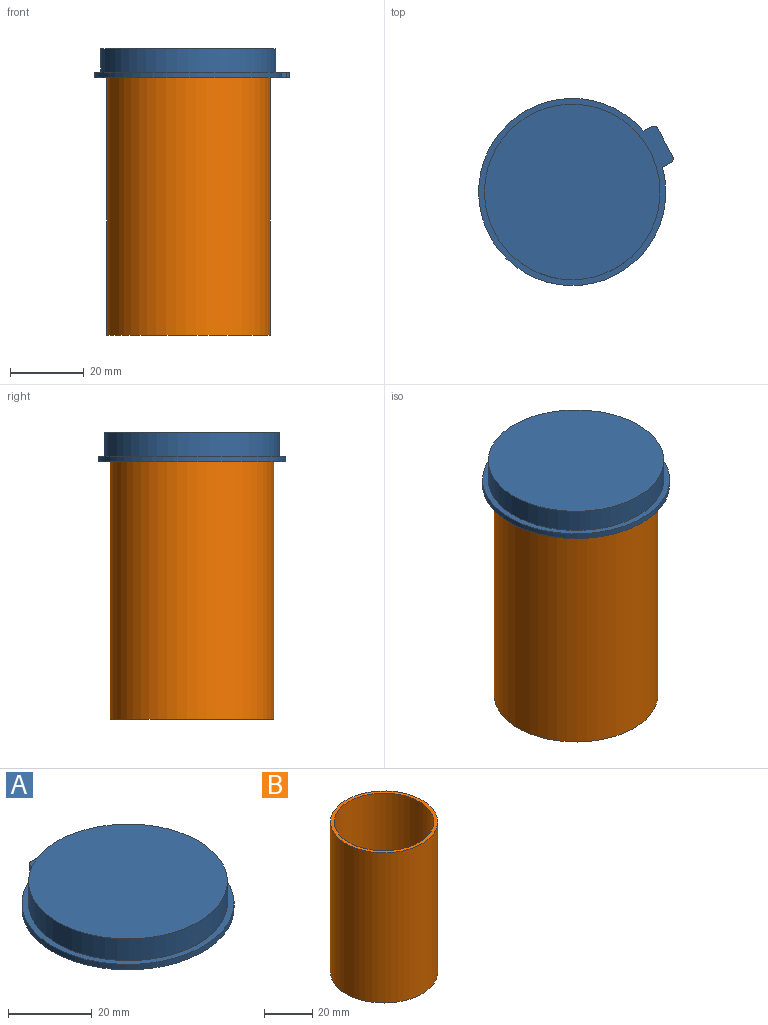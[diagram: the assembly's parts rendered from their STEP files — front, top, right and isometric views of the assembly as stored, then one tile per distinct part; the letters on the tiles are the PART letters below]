
ASSEMBLY  parts=2 mates=1
PART A: 12 faces, bbox 50.8x54x7.9 mm
  f0: cylinder r=23.81mm len=47.63mm, axis (0,0,-1), area 950.1mm2, adj f1,f8
  f1: plane 47.63x47.63mm, normal (0,0,1), area 1781.4mm2, adj f0
  f2: cylinder r=1.27mm len=1.59mm, axis (0,0,-1), area 3.2mm2, adj f3,f7,f8,f9
  f3: plane 8.57x1.59mm, normal (0,1,0), area 13.6mm2, adj f2,f4,f8,f9
  f4: cylinder r=1.27mm len=1.59mm, axis (0,0,-1), area 3.2mm2, adj f3,f5,f8,f9
  f5: plane 2.52x1.59mm, normal (-1,0,0), area 4mm2, adj f4,f6,f8,f9
  f6: cylinder r=25.4mm len=50.8mm, axis (0,0,-1), area 235.6mm2, adj f5,f7,f8,f9
  f7: plane 2.52x1.59mm, normal (1,0,0), area 4mm2, adj f2,f6,f8,f9
  f8: plane 53.98x50.8mm, normal (0,0,1), area 282.3mm2, adj f0,f2,f3,f4,f5,f6,f7
  f9: plane 53.98x50.8mm, normal (0,0,-1), area 511.9mm2, adj f2,f3,f4,f5,f6,f7,f11
  f10: plane 44.45x44.45mm, normal (0,0,-1), area 1551.8mm2, adj f11
  f11: cylinder r=22.23mm len=44.45mm, axis (0,0,-1), area 886.7mm2, adj f9,f10
PART B: 5 faces, bbox 44.5x44.5x76.2 mm
  f0: cylinder r=22.23mm len=76.2mm, axis (0,0,-1), area 10640.9mm2, adj f1,f2
  f1: plane 44.45x44.45mm, normal (0,0,1), area 213.8mm2, adj f0,f3
  f2: plane 44.45x44.45mm, normal (0,0,-1), area 1551.8mm2, adj f0
  f3: cylinder r=20.64mm len=74.61mm, axis (0,0,1), area 9674.9mm2, adj f1,f4
  f4: plane 41.28x41.28mm, normal (0,0,1), area 1338mm2, adj f3
PLACE A rot(axis=(0,0,-1),62deg) t=(16.75,-31.54,69.85)mm
PLACE B t=(-40.7,0,0)mm
MATE cylindrical A.f11 <-> B.f0  axis (0,0,-1) through (0,0,76.2)mm
